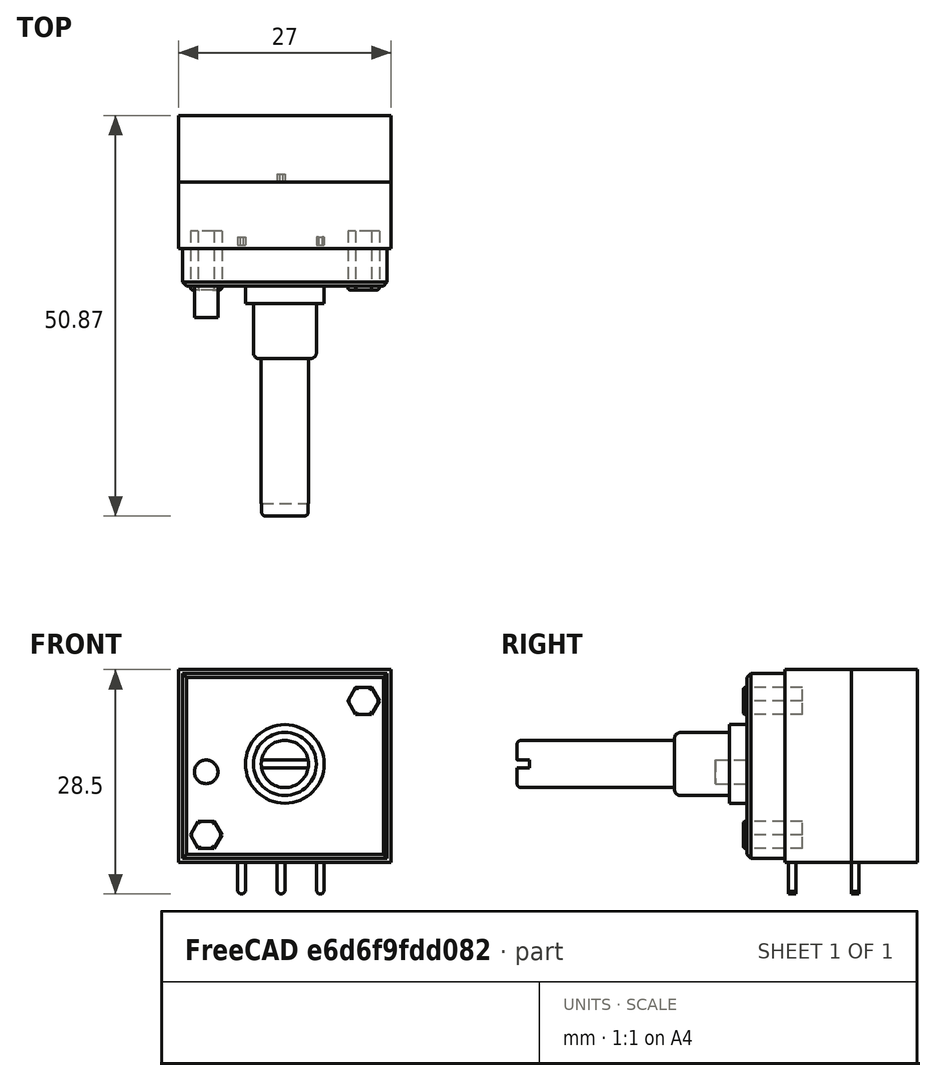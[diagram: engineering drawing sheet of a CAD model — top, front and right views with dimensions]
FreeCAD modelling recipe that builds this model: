
FCSTD DOCUMENT  (FreeCAD 1.0R39319 (Git))
Label: Resistor(ALPS RK27)
License: All rights reserved
LicenseURL: https://en.wikipedia.org/wiki/All_rights_reserved
objects: PartDesign::Body×9, PartDesign::Chamfer×7, PartDesign::AdditiveBox×6, PartDesign::AdditiveCylinder×4, PartDesign::Fillet×4, PartDesign::AdditivePrism×2, PartDesign::SubtractiveBox×1
note: 81 computed .brp shape members not serialized (recipe doc carries the construction recipe); baked Part::Feature solids carry a one-line shape summary decoded from their .brp

FEATURE [PartDesign::AdditiveBox] Box
  AttacherType = Attacher::AttachEngine3D
  Height = 24.5
  Length = 27
  Refine = true
  Suppressed = false
  Width = 8.43
FEATURE [PartDesign::Body] Body  label="Тіло"
  AllowCompound = false
  Group = -> [Box]
  Origin = -> Origin
  Tip = -> Box
FEATURE [PartDesign::AdditiveBox] Box001
  AttacherType = Attacher::AttachEngine3D
  AttachmentSupport = -> [Box]
  Height = 8.43
  Length = 27
  MapMode = 5
  Placement = pos=(0,0,0) rot=(1,0,0;1.5708rad)
  Refine = true
  Suppressed = false
  Width = 24.5
FEATURE [PartDesign::AdditiveBox] Box002
  AttacherType = Attacher::AttachEngine3D
  AttachmentOffset = pos=(0.5,0.5,7) rot=(0,0,1;0rad)
  AttachmentSupport = -> [Box001]
  BaseFeature = -> Box001
  Height = 6.22
  Length = 26
  MapMode = 2
  Placement = pos=(0.5,-7,0.5) rot=(1,0,0;1.5708rad)
  Refine = true
  Suppressed = false
  Width = 23.5
FEATURE [PartDesign::Chamfer] Chamfer
  Angle = 45
  Base = -> Box002 [Edge22,Edge20,Edge18,Edge24]
  BaseFeature = -> Box002
  ChamferType = 0
  FlipDirection = false
  Placement = pos=(0.5,-7,0.5) rot=(1,0,0;1.5708rad)
  Refine = true
  Size = 0.5
  Size2 = 1
  SupportTransform = false
  Suppressed = false
  UseAllEdges = false
FEATURE [PartDesign::Body] Body001  label="Тіло001"
  AllowCompound = false
  Group = -> [Box001,Box002,Chamfer]
  Origin = -> Origin001
  Tip = -> Chamfer
FEATURE [PartDesign::AdditiveCylinder] Cylinder
  Angle = 360
  AttacherType = Attacher::AttachEngine3D
  AttachmentOffset = pos=(13,12,0) rot=(0,0,1;0rad)
  AttachmentSupport = -> [Chamfer]
  FirstAngle = 0
  Height = 2.22
  MapMode = 5
  Placement = pos=(13.5,-13.22,12.5) rot=(1,0,0;1.5708rad)
  Radius = 5
  Refine = true
  SecondAngle = 0
  Suppressed = false
FEATURE [PartDesign::AdditiveCylinder] Cylinder001
  Angle = 360
  AttacherType = Attacher::AttachEngine3D
  AttachmentSupport = -> [Cylinder]
  BaseFeature = -> Cylinder
  FirstAngle = 0
  Height = 7
  MapMode = 5
  Placement = pos=(13.5,-15.44,12.5) rot=(1,0,0;1.5708rad)
  Radius = 4
  Refine = true
  SecondAngle = 0
  Suppressed = false
FEATURE [PartDesign::Fillet] Fillet
  Base = -> Cylinder001 [Edge6]
  BaseFeature = -> Cylinder001
  Placement = pos=(13.5,-15.44,12.5) rot=(1,0,0;1.5708rad)
  Radius = 0.75
  Refine = true
  SupportTransform = false
  Suppressed = false
  UseAllEdges = false
FEATURE [PartDesign::Body] Body002  label="Тіло002"
  AllowCompound = false
  Group = -> [Cylinder,Cylinder001,Fillet]
  Origin = -> Origin002
  Tip = -> Fillet
FEATURE [PartDesign::AdditiveCylinder] Cylinder002
  Angle = 360
  AttacherType = Attacher::AttachEngine3D
  AttachmentSupport = -> [Fillet]
  FirstAngle = 0
  Height = 20
  MapMode = 5
  Placement = pos=(13.5,-22.44,12.5) rot=(1,0,0;1.5708rad)
  Radius = 3
  Refine = true
  SecondAngle = 0
  Suppressed = false
FEATURE [PartDesign::Fillet] Fillet001
  Base = -> Cylinder002 [Edge3]
  BaseFeature = -> Cylinder002
  Placement = pos=(13.5,-22.44,12.5) rot=(1,0,0;1.5708rad)
  Radius = 0.5
  Refine = true
  SupportTransform = false
  Suppressed = false
  UseAllEdges = false
FEATURE [PartDesign::SubtractiveBox] Box003
  AttacherType = Attacher::AttachEngine3D
  AttachmentOffset = pos=(-3.6,-0.5,-1.6) rot=(0,0,1;0rad)
  AttachmentSupport = -> [Fillet001]
  BaseFeature = -> Fillet001
  Height = 1.6
  Length = 7
  MapMode = 5
  Placement = pos=(9.9,-40.84,12) rot=(1,0,0;1.5708rad)
  Refine = true
  Suppressed = false
  Width = 1
FEATURE [PartDesign::AdditiveCylinder] Cylinder003
  Angle = 360
  AttacherType = Attacher::AttachEngine3D
  AttachmentOffset = pos=(3,11,0) rot=(0,0,1;0rad)
  AttachmentSupport = -> [Chamfer]
  BaseFeature = -> Box003
  FirstAngle = 0
  Height = 4
  MapMode = 5
  Placement = pos=(3.5,-13.22,11.5) rot=(1,0,0;1.5708rad)
  Radius = 1.5
  Refine = true
  SecondAngle = 0
  Suppressed = false
FEATURE [PartDesign::Body] Body003  label="Тіло003"
  AllowCompound = false
  Group = -> [Cylinder002,Fillet001,Box003,Cylinder003]
  Origin = -> Origin003
  Tip = -> Cylinder003
FEATURE [PartDesign::AdditiveBox] Box004
  AttacherType = Attacher::AttachEngine3D
  AttachmentOffset = pos=(7,0,0) rot=(0,0,1;0rad)
  AttachmentSupport = -> [Chamfer]
  Height = 4
  Length = 1
  MapMode = 5
  Placement = pos=(7.5,-7,0) rot=(1,0,0;3.14159rad)
  Refine = true
  Suppressed = false
  Width = 1
FEATURE [PartDesign::AdditiveBox] Box005
  AttacherType = Attacher::AttachEngine3D
  AttachmentOffset = pos=(5,-8,0) rot=(0,0,1;0rad)
  AttachmentSupport = -> [Box004]
  Height = 4
  Length = 1
  MapMode = 2
  Placement = pos=(12.5,1,0) rot=(1,0,0;3.14159rad)
  Refine = true
  Suppressed = false
  Width = 1
FEATURE [PartDesign::AdditiveBox] Box006
  AttacherType = Attacher::AttachEngine3D
  AttachmentOffset = pos=(5,8,0) rot=(0,0,1;0rad)
  AttachmentSupport = -> [Box005]
  Height = 4
  Length = 1
  MapMode = 2
  Placement = pos=(17.5,-7,0) rot=(1,0,0;3.14159rad)
  Refine = true
  Suppressed = false
  Width = 1
FEATURE [PartDesign::Chamfer] Chamfer001
  Angle = 45
  Base = -> Box006 [Edge6]
  BaseFeature = -> Box006
  ChamferType = 0
  FlipDirection = false
  Placement = pos=(17.5,-7,1.6e-15) rot=(1,0,0;3.14159rad)
  Refine = true
  Size = 0.3
  Size2 = 1
  SupportTransform = false
  Suppressed = false
  UseAllEdges = false
FEATURE [PartDesign::Chamfer] Chamfer002
  Angle = 45
  Base = -> Chamfer001 [Edge15]
  BaseFeature = -> Chamfer001
  ChamferType = 0
  FlipDirection = false
  Placement = pos=(17.5,-7,1.6e-15) rot=(1,0,0;3.14159rad)
  Refine = true
  Size = 0.3
  Size2 = 1
  SupportTransform = false
  Suppressed = false
  UseAllEdges = false
FEATURE [PartDesign::Body] Body006  label="Тіло006"
  AllowCompound = false
  Group = -> [Box006,Chamfer001,Chamfer002]
  Origin = -> Origin006
  Tip = -> Chamfer002
FEATURE [PartDesign::Chamfer] Chamfer003
  Angle = 45
  Base = -> Box005 [Edge2]
  BaseFeature = -> Box005
  ChamferType = 0
  FlipDirection = false
  Placement = pos=(12.5,1,1.6e-15) rot=(1,0,0;3.14159rad)
  Refine = true
  Size = 0.3
  Size2 = 1
  SupportTransform = false
  Suppressed = false
  UseAllEdges = false
FEATURE [PartDesign::Chamfer] Chamfer004
  Angle = 45
  Base = -> Chamfer003 [Edge15]
  BaseFeature = -> Chamfer003
  ChamferType = 0
  FlipDirection = false
  Placement = pos=(12.5,1,1.6e-15) rot=(1,0,0;3.14159rad)
  Refine = true
  Size = 0.3
  Size2 = 1
  SupportTransform = false
  Suppressed = false
  UseAllEdges = false
FEATURE [PartDesign::Body] Body005  label="Тіло005"
  AllowCompound = false
  Group = -> [Box005,Chamfer003,Chamfer004]
  Origin = -> Origin005
  Tip = -> Chamfer004
FEATURE [PartDesign::Chamfer] Chamfer005
  Angle = 45
  Base = -> Box004 [Edge2]
  BaseFeature = -> Box004
  ChamferType = 0
  FlipDirection = false
  Placement = pos=(7.5,-7,1.6e-15) rot=(1,0,0;3.14159rad)
  Refine = true
  Size = 0.3
  Size2 = 1
  SupportTransform = false
  Suppressed = false
  UseAllEdges = false
FEATURE [PartDesign::Chamfer] Chamfer006
  Angle = 45
  Base = -> Chamfer005 [Edge15]
  BaseFeature = -> Chamfer005
  ChamferType = 0
  FlipDirection = false
  Placement = pos=(7.5,-7,1.6e-15) rot=(1,0,0;3.14159rad)
  Refine = true
  Size = 0.3
  Size2 = 1
  SupportTransform = false
  Suppressed = false
  UseAllEdges = false
FEATURE [PartDesign::Body] Body004  label="Тіло004"
  AllowCompound = false
  Group = -> [Box004,Chamfer005,Chamfer006]
  Origin = -> Origin004
  Tip = -> Chamfer006
FEATURE [PartDesign::AdditivePrism] Prism
  AttacherType = Attacher::AttachEngine3D
  AttachmentOffset = pos=(23,20,-7) rot=(0,0,1;0rad)
  AttachmentSupport = -> [Chamfer]
  Circumradius = 2
  FirstAngle = 0
  Height = 7.5
  MapMode = 5
  Placement = pos=(23.5,-6.22,20.5) rot=(1,0,0;1.5708rad)
  Polygon = 6
  Refine = true
  SecondAngle = 0
  Suppressed = false
FEATURE [PartDesign::Fillet] Fillet002
  Base = -> Prism [Edge10,Edge7,Edge4,Edge18,Edge16,Edge13]
  BaseFeature = -> Prism
  Placement = pos=(23.5,-6.22,20.5) rot=(1,0,0;1.5708rad)
  Radius = 0.3
  Refine = true
  SupportTransform = false
  Suppressed = false
  UseAllEdges = false
FEATURE [PartDesign::Body] Body007  label="Тіло007"
  AllowCompound = false
  Group = -> [Prism,Fillet002]
  Origin = -> Origin007
  Tip = -> Fillet002
FEATURE [PartDesign::AdditivePrism] Prism001
  AttacherType = Attacher::AttachEngine3D
  AttachmentOffset = pos=(3,3,-7) rot=(0,0,1;0rad)
  AttachmentSupport = -> [Chamfer]
  Circumradius = 2
  FirstAngle = 0
  Height = 7.5
  MapMode = 5
  Placement = pos=(3.5,-6.22,3.5) rot=(1,0,0;1.5708rad)
  Polygon = 6
  Refine = true
  SecondAngle = 0
  Suppressed = false
FEATURE [PartDesign::Fillet] Fillet003
  Base = -> Prism001 [Edge4,Edge7,Edge10,Edge13,Edge16,Face8,Edge18]
  BaseFeature = -> Prism001
  Placement = pos=(3.5,-6.22,3.5) rot=(1,0,0;1.5708rad)
  Radius = 0.3
  Refine = true
  SupportTransform = false
  Suppressed = false
  UseAllEdges = false
FEATURE [PartDesign::Body] Body008  label="Тіло008"
  AllowCompound = false
  Group = -> [Prism001,Fillet003]
  Origin = -> Origin008
  Tip = -> Fillet003
